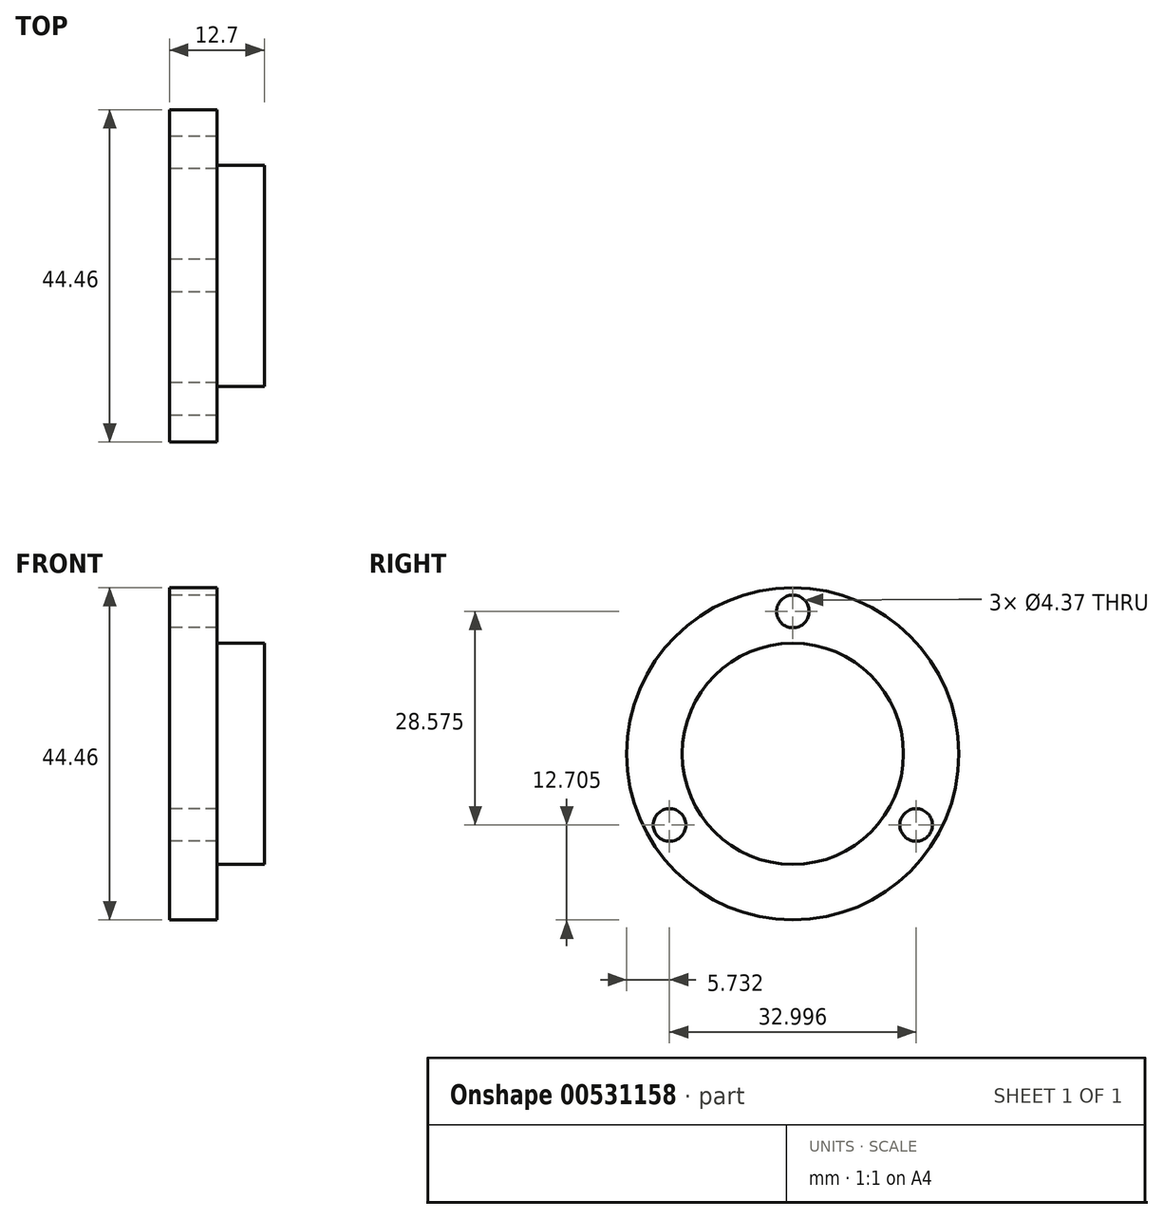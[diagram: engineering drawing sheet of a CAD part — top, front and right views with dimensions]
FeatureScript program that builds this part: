
annotation { "Feature Type Name" : "Feature", "Feature Type Description" : "" }
export const myFeature = defineFeature(function(context is Context, id is Id, definition is map)
    precondition{}
    {
        {
            var Q0;
            Q0=qCreatedBy(makeId("Right.planeOp"),FACE);
            var sketch = newSketch(context, id + "F0", { "sketchPlane" : qUnion([Q0])});
            skCircle(sketch, "E0", {"center": v(0, 0) * mm, "radius": 22.23 * mm});
            skSolve(sketch);
        }
        {
            var Q0;
            Q0 = qSketchRegion(id + "F0", true);
            extrude(context, id + "F1", {"entities" : qUnion([Q0]), "depth" : 6.35 * mm, "offsetDistance" : 25.4 * mm});
        }
        {
            var Q0;
            Q0=makeQuery(id+"F1.opExtrude","CAP_FACE",FACE,{"disambiguationData":[OSD([sQuery(id+"F0.wireOp",EDGE,"E0")])],"isStart":false});
            var sketch = newSketch(context, id + "F2", { "sketchPlane" : qUnion([Q0])});
            skCircle(sketch, "E1", {"center": v(0, 0) * mm, "radius": 14.8 * mm});
            skSolve(sketch);
        }
        {
            var Q0;
            Q0 = qSketchRegion(id + "F2", true);
            extrude(context, id + "F3", {"entities" : qUnion([Q0]), "operationType" : NewBodyOperationType.ADD, "depth" : 6.35 * mm, "offsetDistance" : 25.4 * mm});
        }
        {
            var Q0;
            Q0=makeQuery(id+"F1.opExtrude","CAP_FACE",FACE,{"disambiguationData":[OSD([sQuery(id+"F0.wireOp",EDGE,"E0")])],"isStart":true});
            var sketch = newSketch(context, id + "F4", { "sketchPlane" : qUnion([Q0])});
            skPoint(sketch, "E2.0.midPoint", {"position": v(0, -20.7) * mm});
            skCircle(sketch, "E3", {"center": v(0, 0) * mm, "radius": 19.05 * mm});
            skLineSegment(sketch, "E4", {"start": v(0, 0) * mm, "end": v(0, 19.05) * mm});
            skCircle(sketch, "E5", {"center": v(0, 19.05) * mm, "radius": 2.18 * mm});
            skCircle(sketch, "E6.1.0", {"center": v(-16.5, -9.52) * mm, "radius": 2.18 * mm});
            skCircle(sketch, "E6.2.0", {"center": v(16.5, -9.53) * mm, "radius": 2.18 * mm});
            skSolve(sketch);
        }
        {
            var Q0;
            {var subQ0=sQuery(id+"F4.wireOp",EDGE,"E6.1.0");var subQ1=sQuery(id+"F4.wireOp",EDGE,"E3");var subQ2=makeQuery(id+"F4.imprint","INTERSECT",VERTEX,{"disambiguationData":[OD(0.0)],"derivedFrom":[subQ1,subQ0]});Q0=makeQuery(id+"F4.imprint","IMPRINT",FACE,{"disambiguationData":[TD([[makeQuery(id+"F4.imprint","IMPRINT",EDGE,{"disambiguationData":[TD([[subQ2,-1.0]])],"derivedFrom":subQ1}),1.0]])]});}
            var Q1;
            {var subQ0=sQuery(id+"F4.wireOp",EDGE,"E6.1.0");var subQ1=sQuery(id+"F4.wireOp",EDGE,"E3");var subQ2=makeQuery(id+"F4.imprint","INTERSECT",VERTEX,{"disambiguationData":[OD(0.0)],"derivedFrom":[subQ1,subQ0]});Q1=makeQuery(id+"F4.imprint","IMPRINT",FACE,{"disambiguationData":[TD([[makeQuery(id+"F4.imprint","IMPRINT",EDGE,{"disambiguationData":[TD([[subQ2,-1.0]])],"derivedFrom":subQ1}),-1.0]])]});}
            var Q2;
            {var subQ0=sQuery(id+"F4.wireOp",EDGE,"E6.2.0");var subQ1=sQuery(id+"F4.wireOp",EDGE,"E3");var subQ2=makeQuery(id+"F4.imprint","INTERSECT",VERTEX,{"disambiguationData":[OD(0.0)],"derivedFrom":[subQ1,subQ0]});Q2=makeQuery(id+"F4.imprint","IMPRINT",FACE,{"disambiguationData":[TD([[makeQuery(id+"F4.imprint","IMPRINT",EDGE,{"disambiguationData":[TD([[subQ2,-1.0]])],"derivedFrom":subQ1}),1.0]])]});}
            var Q3;
            {var subQ0=sQuery(id+"F4.wireOp",EDGE,"E6.2.0");var subQ1=sQuery(id+"F4.wireOp",EDGE,"E3");var subQ2=makeQuery(id+"F4.imprint","INTERSECT",VERTEX,{"disambiguationData":[OD(0.0)],"derivedFrom":[subQ1,subQ0]});Q3=makeQuery(id+"F4.imprint","IMPRINT",FACE,{"disambiguationData":[TD([[makeQuery(id+"F4.imprint","IMPRINT",EDGE,{"disambiguationData":[TD([[subQ2,-1.0]])],"derivedFrom":subQ1}),-1.0]])]});}
            var Q4;
            {var subQ0=sQuery(id+"F4.wireOp",EDGE,"E3");var subQ1=makeQuery(id+"F4.imprint","INTERSECT",VERTEX,{"derivedFrom":[subQ0,sQuery(id+"F4.wireOp",EDGE,"E4")]});Q4=makeQuery(id+"F4.imprint","IMPRINT",FACE,{"disambiguationData":[TD([[makeQuery(id+"F4.imprint","IMPRINT",EDGE,{"disambiguationData":[TD([[subQ1,1.0]])],"derivedFrom":subQ0}),-1.0]])]});}
            var Q5;
            {var subQ0=sQuery(id+"F4.wireOp",EDGE,"E4");var subQ1=sQuery(id+"F4.wireOp",EDGE,"E3");var subQ2=makeQuery(id+"F4.imprint","INTERSECT",VERTEX,{"derivedFrom":[subQ1,subQ0]});Q5=makeQuery(id+"F4.imprint","IMPRINT",FACE,{"disambiguationData":[TD([[makeQuery(id+"F4.imprint","IMPRINT",EDGE,{"disambiguationData":[TD([[subQ2,1.0]])],"derivedFrom":subQ1}),1.0]])]});}
            var Q6;
            {var subQ0=sQuery(id+"F4.wireOp",EDGE,"E4");var subQ1=sQuery(id+"F4.wireOp",EDGE,"E3");var subQ2=makeQuery(id+"F4.imprint","INTERSECT",VERTEX,{"derivedFrom":[subQ1,subQ0]});Q6=makeQuery(id+"F4.imprint","IMPRINT",FACE,{"disambiguationData":[TD([[makeQuery(id+"F4.imprint","IMPRINT",EDGE,{"disambiguationData":[TD([[subQ2,-1.0]])],"derivedFrom":subQ1}),1.0]])]});}
            extrude(context, id + "F5", {"entities" : qUnion([Q0, Q1, Q2, Q3, Q4, Q5, Q6]), "operationType" : NewBodyOperationType.REMOVE, "oppositeDirection" : true, "depth" : 25.4 * mm, "offsetDistance" : 25.4 * mm});
        }
    });
